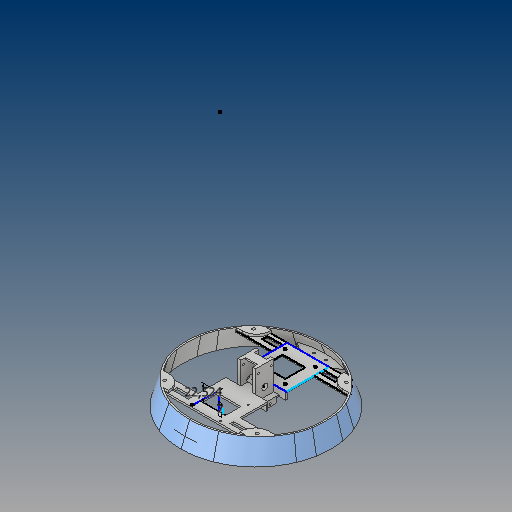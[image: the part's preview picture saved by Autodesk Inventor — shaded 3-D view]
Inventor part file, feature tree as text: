
AUTODESK INVENTOR PART (.ipt)
format: ipt  version: 2017 (Build 210142000, 142)  size: 1,515,008 bytes
history: native  units: mm
features: sketch x35, extrude x30, projected_geometry x7, plane x3, fillet x1, loft x1, mirror x1, shell x1, other x1
ambient origin geometry x8: Origin, YZ Plane, XZ Plane, XY Plane, X Axis, Y Axis, Z Axis, Center Point
bodies: Solid1 (feature_tree)
feature tree (80):
  extrude  "Extrusion1"  Depth=35.0mm
  extrude  "Extrusion2"  Depth=9.0mm TaperAngle=0.0deg
  extrude  "Extrusion6"  Depth=70.0mm TaperAngle=0.0deg
  extrude  "Extrusion9"  Depth=10.0mm
  extrude  "Extrusion11"  Depth=200.0mm
  fillet  "Fillet2"  [1 undecoded]
  sketch  "Sketch29"  dims[d72=0.0mm d73=90.0deg d81=2.0mm d82=22.524mm]
  plane  "Work Plane8"
  loft  "Loft1"
  mirror  "Mirror8"
  shell  "Shell3"  Thickness=22.524mm
  sketch  "Sketch36"  dims[d95=7.0mm d96=-15.524mm]
  plane  "Work Plane9"
  extrude  "Extrusion16"  Depth=2.5mm TaperAngle=0.0deg
  plane  "Work Plane10"
  extrude  "Extrusion17"  [1 undecoded]
  extrude  "Extrusion18"  Depth=1.5mm TaperAngle=0.0deg
  sketch  "Sketch40"  dims[d117=6.25mm d118=43.5mm]
  extrude  "Extrusion19"  Depth=3.0mm TaperAngle=0.0deg
  extrude  "Extrusion20"  Depth=173.3463mm TaperAngle=0.0deg
  extrude  "Extrusion21"  Depth=43.5mm
  extrude  "Extrusion22"  Depth=2.0mm
  extrude  "Extrusion23"  Depth=2.0mm
  extrude  "Extrusion24"  Depth=12.0mm
  extrude  "Extrusion25"  Depth=16.0mm
  extrude  "Extrusion26"  Depth=10.0mm TaperAngle=0.0deg
  extrude  "Extrusion27"  Depth=4.0mm
  extrude  "Extrusion28"  Depth=6.0mm
  extrude  "Extrusion29"  Depth=12.0mm
  extrude  "Extrusion30"  Depth=2.5mm
  extrude  "Extrusion31"  Depth=25.0mm TaperAngle=0.0deg
  extrude  "Extrusion32"  Depth=8.0mm
  extrude  "Extrusion33"  Depth=2.0mm
  extrude  "Extrusion34"  Depth=28.0mm
  extrude  "Extrusion36"  Depth=18.0mm
  extrude  "Extrusion37"  Depth=8.0mm TaperAngle=0.0deg
  extrude  "Extrusion38"  Depth=9.0mm
  extrude  "Extrusion39"  Depth=5.0mm
  extrude  "Extrusion40"  Depth=3.0mm
  extrude  "Extrusion41"  Depth=6.0mm TaperAngle=0.0deg
  sketch  "Sketch71"  dims[d185=3.0mm d186=3.0mm d187=6.0mm d188=0.0mm d189=3.0mm d190=40.0mm d191=3.0mm d192=40.0mm d193=3.0mm d194=40.0mm d195=3.0mm d196=10.0mm d197=0.0mm d200=145.0mm d201=0.0mm d203=145.0mm d204=0.0mm d214=3.0mm d215=0.0mm d216=7.5mm d217=4.0mm d218=4.0mm d219=4.0mm d220=4.0mm d221=30.0mm d222=0.0mm d227=3.0mm d228=0.0mm d229=10.0mm d230=0.0mm]
  sketch  "Sketch1"  dims[d0=63.0mm d1=0.0mm d2=35.0mm]
  sketch  "Sketch3"  dims[d3=150.0mm d4=9.0mm d5=0.0mm]
  sketch  "Sketch12"  dims[d30=250.0mm d31=0.0mm d48=70.0mm d49=0.0mm]
  sketch  "Sketch17"  dims[d53=70.0mm d54=0.0mm d55=10.0mm]
  sketch  "Sketch20"  dims[d68=-347.0mm d69=200.0mm d70=0.0mm d71=90.0deg]
  projected_geometry  "Projected Loop9"
  sketch  "Sketch30"  dims[d83=-324.476mm d93=2.5mm d94=0.0mm]
  other  "Edges1"
  sketch  "Sketch37"  dims[d102=4.0mm d103=0.0mm d104=1.5mm d105=0.0mm]
  sketch  "Sketch38"  dims[d106=2.0mm d107=0.0mm d111=3.0mm d112=0.0mm]
  sketch  "Sketch39"  dims[d113=12.0mm d114=0.0mm d115=173.3463mm d116=0.0mm]
  projected_geometry  "Projected Loop13"
  projected_geometry  "Projected Loop14"
  sketch  "Sketch41"  dims[d119=43.5mm d129=2.0mm]
  sketch  "Sketch43"  dims[d130=2.0mm d131=2.0mm]
  sketch  "Sketch44"  dims[d132=3.0mm d133=0.0mm d134=12.0mm]
  projected_geometry  "Projected Loop15"
  projected_geometry  "Projected Loop16"
  sketch  "Sketch45"  dims[d135=24.0mm d136=16.0mm]
  sketch  "Sketch46"  dims[d137=16.0mm d138=10.0mm d139=0.0mm]
  sketch  "Sketch47"  dims[d140=4.0mm d141=4.0mm]
  sketch  "Sketch48"  dims[d142=30.0mm d143=0.0mm d144=6.0mm]
  sketch  "Sketch49"  dims[d145=6.0mm d146=12.0mm]
  sketch  "Sketch50"  dims[d147=2.0mm d148=0.0mm d152=2.5mm]
  sketch  "Sketch51"  dims[d153=2.5mm d154=25.0mm d155=0.0mm]
  sketch  "Sketch52"  dims[d156=3.0mm d157=8.0mm]
  sketch  "Sketch53"  dims[d158=40.0mm d159=0.0mm d160=2.0mm]
  sketch  "Sketch54"  dims[d161=18.0mm d162=28.0mm]
  sketch  "Sketch55"  dims[d163=2.0mm d164=18.0mm]
  sketch  "Sketch56"  dims[d165=28.0mm d166=8.0mm d167=0.0mm]
  sketch  "Sketch57"  dims[d168=9.0mm d169=9.0mm]
  sketch  "Sketch59"  dims[d170=2.0mm d171=0.0mm d172=5.0mm]
  sketch  "Sketch61"  dims[d173=10.0mm d174=3.0mm]
  sketch  "Sketch63"  dims[d176=10.0mm d178=6.0mm d179=0.0mm]
  sketch  "Sketch64"  dims[d181=60.0mm d182=0.0mm]
  sketch  "Sketch66"  dims[d183=3.0mm]
  sketch  "Sketch67"  dims[d184=3.0mm]
  projected_geometry  "Projected Loop18"
  projected_geometry  "Projected Loop24"
note: 2 required parameter values undecoded (feature->parameter linkage not recoverable at this tier; creation-order binding heuristic only, values carry confidence <= 0.55)
